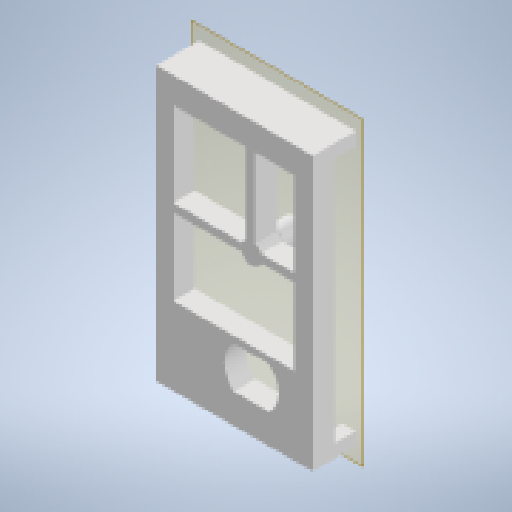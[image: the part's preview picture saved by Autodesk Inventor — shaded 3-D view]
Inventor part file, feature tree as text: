
AUTODESK INVENTOR PART (.ipt)
format: ipt  version: 2023 (Build 270158000, 158)  size: 164,864 bytes
history: native  units: mm
features: other x4, extrude x2, plane x1, sketch x1, reference x1, projected_geometry x1
ambient origin geometry x8: Origin, YZ Plane, XZ Plane, XY Plane, X Axis, Y Axis, Z Axis, Center Point
bodies: Solid1 (feature_tree)
feature tree (10):
  plane  "Work Plane1"
  extrude  "Extrusion1"  Depth=0.2mm
  extrude  "Extrusion2"  Depth=8.0mm TaperAngle=0.0deg
  sketch  "Sketch2"  dims[d7=8.0mm d8=0.0mm d9=0.2mm d10=8.0mm d11=0.0mm d15=20.0mm d17=91.422mm d18=20.0mm d20=48.171mm]
  reference  "Reference5"
  projected_geometry  "Projected Loop1"
  parser-record x1  (decoder bookkeeping rows leaked as tree rows — omitted from the tree; the rows remain in map.json)
  other  "doorLockAssembly_V4.iam"
  other  "motor:1"
  other  "housingPlate:1"
note: 1 file-system path scrubbed to <path> (originals preserved in map.json)
